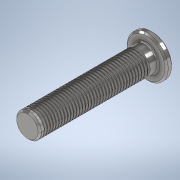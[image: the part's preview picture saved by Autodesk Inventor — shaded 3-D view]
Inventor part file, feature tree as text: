
AUTODESK INVENTOR PART (.ipt)
format: ipt  version: 2021 (Build 250183000, 183)  size: 790,016 bytes
history: native  units: in
note: dims shown in document units (in); Inventor stores cm internally (conversion verified against a paired STEP export)
features: sketch x5, extrude x4, chamfer x3, fillet x2, helix x1, projected_geometry x1
ambient origin geometry x8: Origin, YZ Plane, XZ Plane, XY Plane, X Axis, Y Axis, Z Axis, Center Point
bodies: Solid2 (feature_tree)
feature tree (16):
  extrude  "Extrusion3"  Depth=0.2846in TaperAngle=0.0deg
  chamfer  "Chamfer1"  Distance=0.0039in Angle=45.0deg
  extrude  "Extrusion4"  Depth=0.0157in TaperAngle=0.0deg
  fillet  "Fillet1"  Radius=0.0039in
  chamfer  "Chamfer2"  Distance=0.0039in Angle=45.0deg
  chamfer  "Chamfer3"  Distance=0.0039in Angle=45.0deg
  extrude  "Extrusion5"  Depth=0.0118in
  helix  "Coil1"  [1 undecoded]
  fillet  "Fillet3"  Radius=0.0591in
  extrude  "Extrusion6"  TaperAngle=60.0deg  [1 undecoded]
  sketch  "Sketch3"  dims[d6=0.0591in d7=0.2846in d8=0.0in d9=0.0039in d10=0.0787in d11=45.0deg]
  sketch  "Sketch4"  dims[d12=0.0984in d13=0.0157in d14=0.0in d15=0.0039in d17=0.0039in d18=0.0787in d19=45.0deg d20=0.0039in d21=0.0787in d22=45.0deg]
  sketch  "Sketch5"  dims[d23=0.0079in d24=0.0in d25=0.0118in d26=0.0118in d27=0.0591in]
  sketch  "Sketch6"  dims[d32=0.0197in d33=60.0deg]
  sketch  "Sketch7"  dims[d35=0.0039in d36=0.002in d37=0.0071in d38=0.3937in d39=14.1732in d40=0.0in d41=90.0deg d42=90.0deg d43=0.0in d44=0.0in d45=0.0039in d46=0.0236in d47=0.0in]
  projected_geometry  "Projected Loop1"
note: 2 required parameter values undecoded (feature->parameter linkage not recoverable at this tier; creation-order binding heuristic only, values carry confidence <= 0.55)
